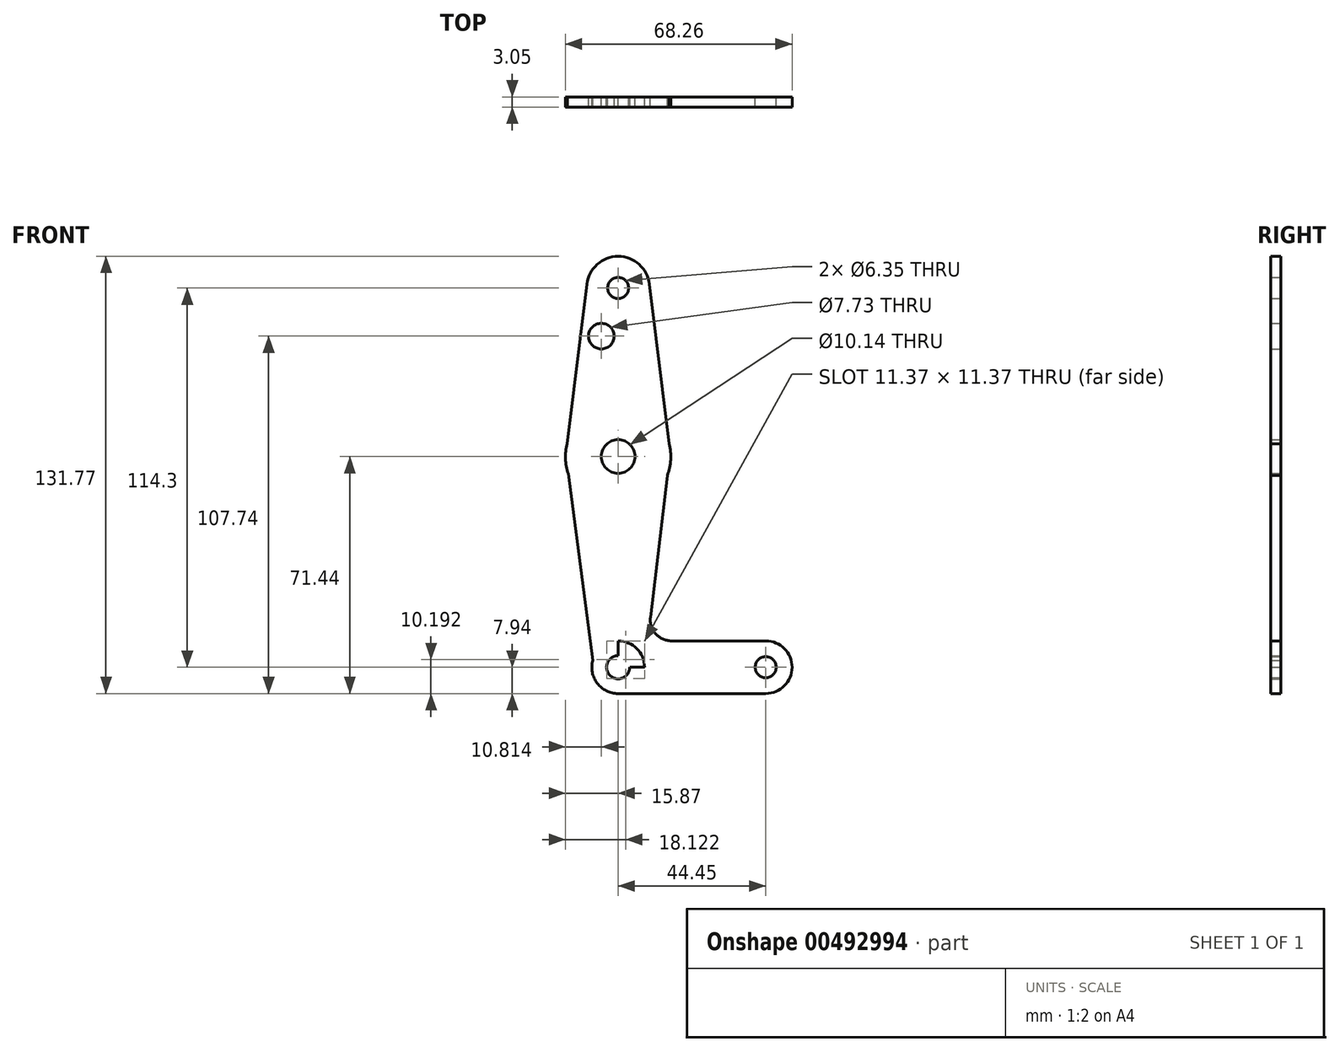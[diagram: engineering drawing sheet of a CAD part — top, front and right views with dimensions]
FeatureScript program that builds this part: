
annotation { "Feature Type Name" : "Feature", "Feature Type Description" : "" }
export const myFeature = defineFeature(function(context is Context, id is Id, definition is map)
    precondition{}
    {
        {
            var Q0;
            Q0=qCreatedBy(makeId("Front.planeOp"),FACE);
            var sketch = newSketch(context, id + "F0", { "sketchPlane" : qUnion([Q0])});
            skLineSegment(sketch, "E0", {"start": v(0, 0) * mm, "end": v(0, 114.3) * mm});
            skLineSegment(sketch, "E1", {"start": v(0, 0) * mm, "end": v(44.45, 0) * mm});
            skCircle(sketch, "E2", {"center": v(0, 114.3) * mm, "radius": 9.53 * mm});
            skCircle(sketch, "E3", {"center": v(0, 63.5) * mm, "radius": 15.88 * mm});
            skCircle(sketch, "E4", {"center": v(0, 0) * mm, "radius": 7.94 * mm});
            skCircle(sketch, "E5", {"center": v(44.45, 0) * mm, "radius": 7.94 * mm});
            skLineSegment(sketch, "E6", {"start": v(15.88, 63.5) * mm, "end": v(9.45, 115.47) * mm});
            skLineSegment(sketch, "E7", {"start": v(-15.88, 63.5) * mm, "end": v(-9.45, 115.47) * mm});
            skLineSegment(sketch, "E8", {"start": v(14.82, 57.81) * mm, "end": v(9.73, 15.04) * mm});
            skLineSegment(sketch, "E9", {"start": v(16.03, 7.94) * mm, "end": v(44.45, 7.94) * mm});
            skLineSegment(sketch, "E10", {"start": v(0, -7.94) * mm, "end": v(44.45, -7.94) * mm});
            skPoint(sketch, "E11.end.orphan", {"position": v(-7.99, 0) * mm});
            skCircle(sketch, "E12", {"center": v(0, 114.3) * mm, "radius": 3.18 * mm});
            skCircle(sketch, "E13", {"center": v(-5.06, 99.8) * mm, "radius": 3.86 * mm});
            skLineSegment(sketch, "E14", {"start": v(-15.01, 58.33) * mm, "end": v(-7.66, 2.1) * mm});
            skCircle(sketch, "E15", {"center": v(0, 63.5) * mm, "radius": 5.07 * mm});
            skCircle(sketch, "E16", {"center": v(0, 0) * mm, "radius": 3.5 * mm});
            skCircle(sketch, "E17", {"center": v(44.45, 0) * mm, "radius": 3.18 * mm});
            skPoint(sketch, "E18.newPointB", {"position": v(0, 7.94) * mm});
            skArc(sketch, "E18.filletArc", {"start": v(9.73, 15.04) * mm, "mid": v(11.29, 10.07) * mm, "end": v(16.03, 7.94) * mm});
            skSolve(sketch);
        }
        {
            var Q0;
            Q0 = qSketchRegion(id + "F0", true);
            extrude(context, id + "F1", {"entities" : qUnion([Q0]), "depth" : 3.05 * mm});
        }
    });
